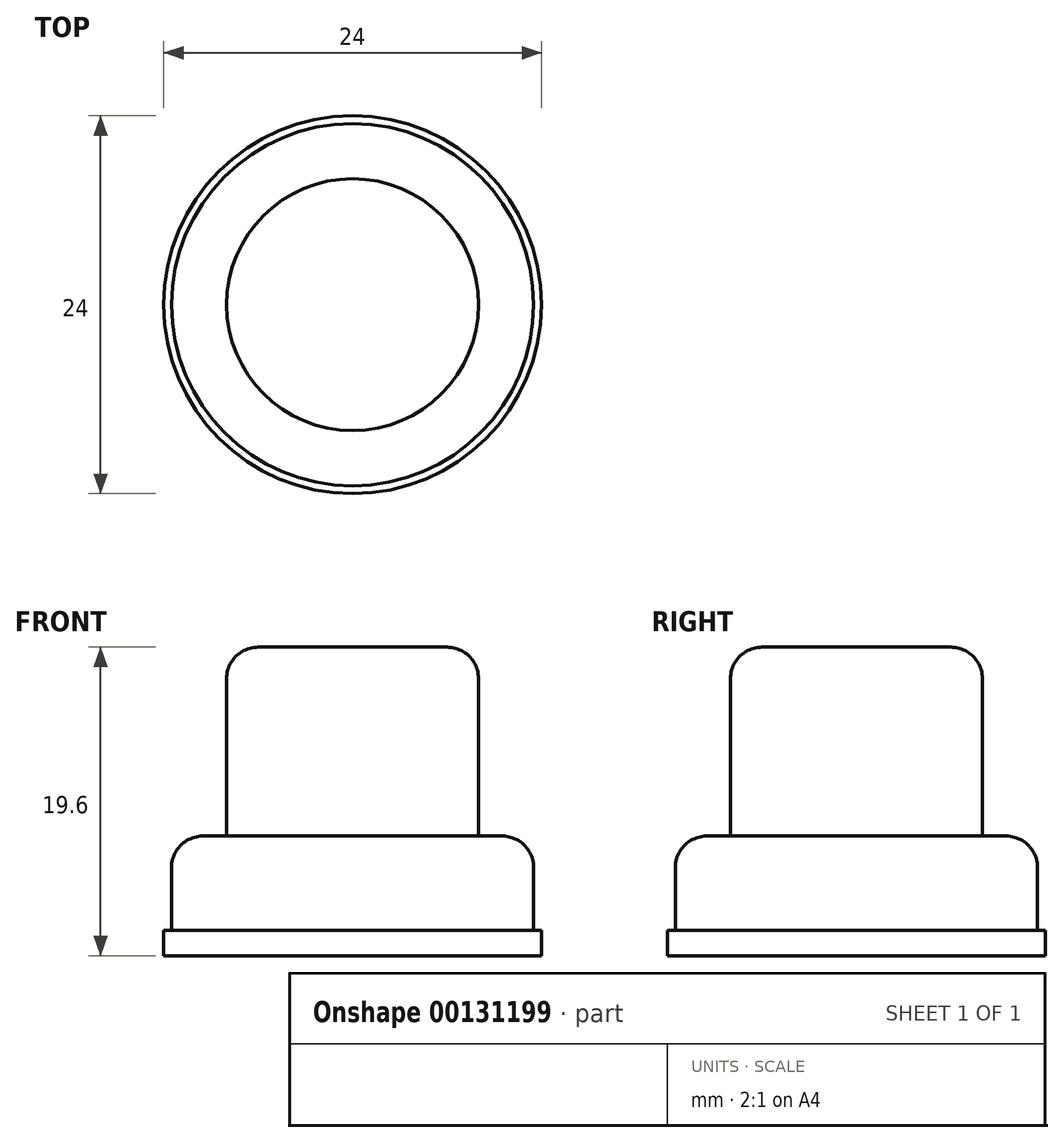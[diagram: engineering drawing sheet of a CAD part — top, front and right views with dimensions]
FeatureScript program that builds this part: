
annotation { "Feature Type Name" : "Feature", "Feature Type Description" : "" }
export const myFeature = defineFeature(function(context is Context, id is Id, definition is map)
    precondition{}
    {
        {
            var Q0;
            Q0=qCreatedBy(makeId("Top.planeOp"),FACE);
            var sketch = newSketch(context, id + "F0", { "sketchPlane" : qUnion([Q0])});
            skCircle(sketch, "E0", {"center": v(0, 0) * mm, "radius": 12 * mm});
            skSolve(sketch);
        }
        {
            var Q0;
            Q0=makeQuery(id+"F0.imprint","IMPRINT",FACE,{"disambiguationData":[TD([[makeQuery(id+"F0.imprint","IMPRINT",EDGE,{"derivedFrom":sQuery(id+"F0.wireOp",EDGE,"E0")}),1.0]])]});
            extrude(context, id + "F1", {"entities" : qUnion([Q0]), "depth" : 1.6 * mm});
        }
        {
            var Q0;
            Q0=makeQuery(id+"F1.opExtrude","CAP_FACE",FACE,{"disambiguationData":[OSD([sQuery(id+"F0.wireOp",EDGE,"E0")])],"isStart":false});
            var sketch = newSketch(context, id + "F2", { "sketchPlane" : qUnion([Q0])});
            skCircle(sketch, "E1", {"center": v(0, 0) * mm, "radius": 11.5 * mm});
            skSolve(sketch);
        }
        {
            var Q0;
            Q0=makeQuery(id+"F2.imprint","IMPRINT",FACE,{"disambiguationData":[TD([[makeQuery(id+"F2.imprint","IMPRINT",EDGE,{"derivedFrom":sQuery(id+"F2.wireOp",EDGE,"E1")}),1.0]])]});
            extrude(context, id + "F3", {"entities" : qUnion([Q0]), "operationType" : NewBodyOperationType.ADD, "depth" : 6 * mm});
        }
        {
            var Q0;
            Q0=makeQuery(id+"F3.opExtrude","CAP_FACE",FACE,{"disambiguationData":[OSD([sQuery(id+"F2.wireOp",EDGE,"E1")])],"isStart":false});
            var sketch = newSketch(context, id + "F4", { "sketchPlane" : qUnion([Q0])});
            skCircle(sketch, "E2", {"center": v(0, 0) * mm, "radius": 8 * mm});
            skSolve(sketch);
        }
        {
            var Q0;
            Q0=makeQuery(id+"F4.imprint","IMPRINT",FACE,{"disambiguationData":[TD([[makeQuery(id+"F4.imprint","IMPRINT",EDGE,{"derivedFrom":sQuery(id+"F4.wireOp",EDGE,"E2")}),1.0]])]});
            extrude(context, id + "F5", {"entities" : qUnion([Q0]), "operationType" : NewBodyOperationType.ADD, "depth" : 12 * mm});
        }
        {
            var Q0;
            Q0=makeQuery(id+"F3.opExtrude","CAP_EDGE",EDGE,{"disambiguationData":[OSD([sQuery(id+"F2.wireOp",EDGE,"E1")])],"isStart":false});
            var Q1;
            Q1=makeQuery(id+"F5.opExtrude","CAP_EDGE",EDGE,{"disambiguationData":[OSD([sQuery(id+"F4.wireOp",EDGE,"E2")])],"isStart":false});
            fillet(context, id + "F6", {"entities" : qUnion([Q0, Q1]), "radius" : 2 * mm, "tangentPropagation" : true, "allowEdgeOverflow" : false});
        }
    });
